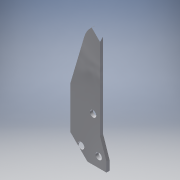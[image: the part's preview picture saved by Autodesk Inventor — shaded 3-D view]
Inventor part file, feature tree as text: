
AUTODESK INVENTOR PART (.ipt)
format: ipt  version: 2016 (Build 200138000, 138)  size: 211,968 bytes
history: native  units: in
note: dims shown in document units (in); Inventor stores cm internally (conversion verified against a paired STEP export)
features: reference x7, extrude x6, sketch x6, projected_geometry x3, fillet x1
ambient origin geometry x8: Origin, YZ Plane, XZ Plane, XY Plane, X Axis, Y Axis, Z Axis, Center Point
bodies: Solid1 (feature_tree)
feature tree (23):
  extrude  "Extrusion1"  Depth=0.26in
  extrude  "Extrusion2"  Depth=1.0in
  extrude  "Extrusion4"  Depth=1.0in
  extrude  "Extrusion5"  Depth=1.0in TaperAngle=0.0deg
  extrude  "Extrusion6"  Depth=0.125in
  fillet  "Fillet1"  Radius=6.1in
  extrude  "Extrusion7"  TaperAngle=0.0deg  [1 undecoded]
  sketch  "Sketch1"  dims[d1=0.26in d2=0.26in]
  reference  "Reference1"
  reference  "Reference2"
  sketch  "Sketch2"  dims[d3=1.0in d6=0.6in]
  sketch  "Sketch3"  dims[d7=0.6in d8=1.0in]
  projected_geometry  "Projected Loop1"
  reference  "Reference3"
  reference  "Reference4"
  sketch  "Sketch4"  dims[d9=0.125in d10=0.0in d11=1.0in d12=0.0in]
  reference  "Reference5"
  projected_geometry  "Projected Loop2"
  sketch  "Sketch5"  dims[d15=0.125in d16=0.0in d17=0.26in d18=6.1in]
  reference  "Reference6"
  sketch  "Sketch6"  dims[d19=0.26in d20=0.0in d21=0.26in d22=0.0in d23=0.25in d24=0.125in d25=0.0in]
  reference  "Reference7"
  projected_geometry  "Projected Loop3"
note: 1 required parameter value undecoded (feature->parameter linkage not recoverable at this tier; creation-order binding heuristic only, values carry confidence <= 0.55)
